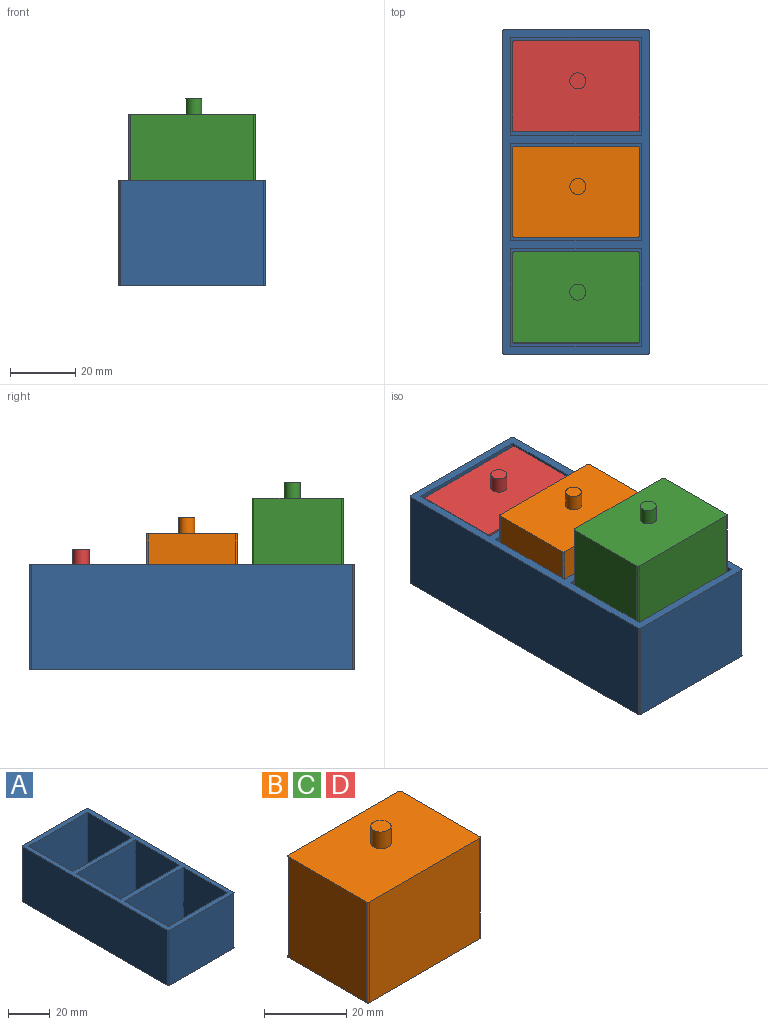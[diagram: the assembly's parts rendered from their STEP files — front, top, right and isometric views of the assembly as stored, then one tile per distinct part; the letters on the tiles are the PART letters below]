
ASSEMBLY  parts=4 mates=3
PART A: 25 faces, bbox 45x100x32.5 mm
  f0: plane 99x32.5mm, normal (-1,0,0), area 3217.5mm2, adj f4,f17,f21,f24
  f1: plane 44x32.5mm, normal (0,-1,0), area 1430mm2, adj f4,f17,f21,f22
  f2: plane 99x32.5mm, normal (1,0,0), area 3217.5mm2, adj f4,f17,f22,f23
  f3: plane 44x32.5mm, normal (0,1,0), area 1430mm2, adj f4,f17,f23,f24
  f4: plane 100x45mm, normal (0,0,-1), area 4499.8mm2, adj f0,f1,f2,f3,f21,f22,f23,f24
  f5: plane 40x30mm, normal (0,1,0), area 1200mm2, adj f6,f16,f17,f18
  f6: plane 30x30mm, normal (1,0,0), area 900mm2, adj f5,f7,f17,f18
  f7: plane 40x30mm, normal (0,-1,0), area 1200mm2, adj f6,f16,f17,f18
  f8: plane 40x30mm, normal (0,1,0), area 1200mm2, adj f9,f14,f17,f19
  f9: plane 30x30mm, normal (1,0,0), area 900mm2, adj f8,f10,f17,f19
  f10: plane 40x30mm, normal (0,-1,0), area 1200mm2, adj f9,f14,f17,f19
  f11: plane 40x30mm, normal (0,1,0), area 1200mm2, adj f12,f15,f17,f20
  f12: plane 30x30mm, normal (1,0,0), area 900mm2, adj f11,f13,f17,f20
  f13: plane 40x30mm, normal (0,-1,0), area 1200mm2, adj f12,f15,f17,f20
  f14: plane 30x30mm, normal (-1,0,0), area 900mm2, adj f8,f10,f17,f19
  f15: plane 30x30mm, normal (-1,0,0), area 900mm2, adj f11,f13,f17,f20
  f16: plane 30x30mm, normal (-1,0,0), area 900mm2, adj f5,f7,f17,f18
  f17: plane 100x45mm, normal (0,0,1), area 899.8mm2, adj f0,f1,f2,f3,f5,f6,f7,f8
  f18: plane 40x30mm, normal (0,0,1), area 1200mm2, adj f5,f6,f7,f16
  f19: plane 40x30mm, normal (0,0,1), area 1200mm2, adj f8,f9,f10,f14
  f20: plane 40x30mm, normal (0,0,1), area 1200mm2, adj f11,f12,f13,f15
  f21: cylinder r=0.5mm len=32.5mm, axis (0,0,-1), area 25.5mm2, adj f0,f1,f4,f17
  f22: cylinder r=0.5mm len=32.5mm, axis (0,0,1), area 25.5mm2, adj f1,f2,f4,f17
  f23: cylinder r=0.5mm len=32.5mm, axis (0,0,-1), area 25.5mm2, adj f2,f3,f4,f17
  f24: cylinder r=0.5mm len=32.5mm, axis (0,0,1), area 25.5mm2, adj f0,f3,f4,f17
PART B: 17 faces, bbox 39x28x35 mm
  f0: plane 34x25mm, normal (0,1,0), area 850mm2, adj f1,f2,f4,f10
  f1: plane 25.5x25mm, normal (-1,0,0), area 637.5mm2, adj f0,f3,f4,f10
  f2: plane 25.5x25mm, normal (1,0,0), area 637.5mm2, adj f0,f3,f4,f10
  f3: plane 38x30mm, normal (0,1,0), area 290mm2, adj f1,f2,f4,f5,f9,f10,f15,f16
  f4: plane 34x25.5mm, normal (0,0,1), area 867mm2, adj f0,f1,f2,f3
  f5: plane 39x28mm, normal (0,0,-1), area 1091.8mm2, adj f3,f6,f7,f8,f13,f14,f15,f16
  f6: plane 30x27mm, normal (-1,0,0), area 810mm2, adj f5,f9,f13,f16
  f7: plane 38x30mm, normal (0,-1,0), area 1140mm2, adj f5,f9,f13,f14
  f8: plane 30x27mm, normal (1,0,0), area 810mm2, adj f5,f9,f14,f15
  f9: plane 39x28mm, normal (0,0,1), area 1072.6mm2, adj f3,f6,f7,f8,f11,f13,f14,f15
  f10: plane 34x25.5mm, normal (0,0,-1), area 867mm2, adj f0,f1,f2,f3
  f11: cylinder r=2.47mm len=5mm, axis (0,0,-1), area 77.6mm2, adj f9,f12
  f12: plane 4.94x4.94mm, normal (0,0,1), area 19.2mm2, adj f11
  f13: cylinder r=0.5mm len=30mm, axis (0,0,1), area 23.6mm2, adj f5,f6,f7,f9
  f14: cylinder r=0.5mm len=30mm, axis (0,0,-1), area 23.6mm2, adj f5,f7,f8,f9
  f15: cylinder r=0.5mm len=30mm, axis (0,0,1), area 23.6mm2, adj f3,f5,f8,f9
  f16: cylinder r=0.5mm len=30mm, axis (0,0,-1), area 23.6mm2, adj f3,f5,f6,f9
PART C: same geometry as B
PART D: same geometry as B
PLACE A t=(23.59,-9.04,2.1)mm fixed
PLACE B t=(-28.95,18.34,11.43)mm
PLACE C t=(-28.95,-14.16,22.39)mm
PLACE D t=(-28.95,50.84,1.79)mm
MATE slider D.f5 <-> A.f20  axis (0,0,-1) through (43.59,70.96,1.79)mm
MATE slider A.f18 <-> C.f5  axis (0,0,1) through (43.59,5.96,2.1)mm
MATE slider B.f5 <-> A.f19  axis (0,0,-1) through (43.59,38.46,11.43)mm
